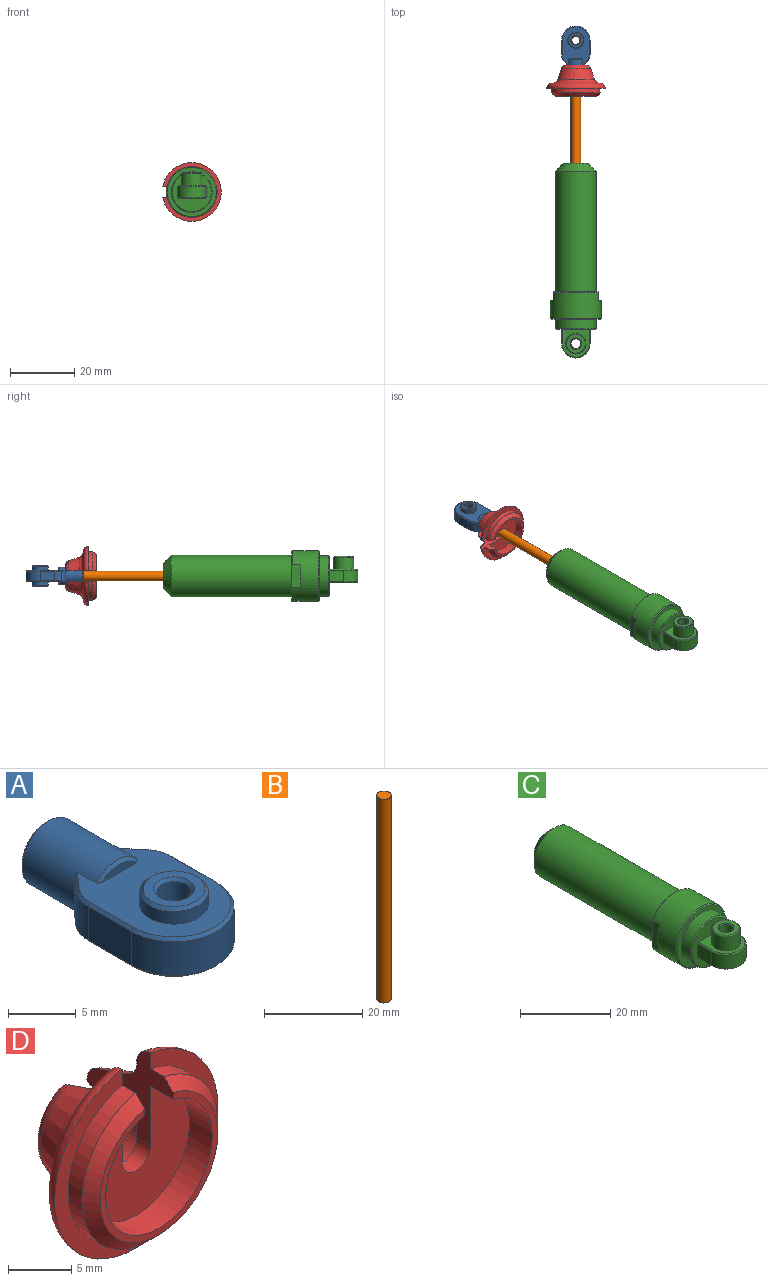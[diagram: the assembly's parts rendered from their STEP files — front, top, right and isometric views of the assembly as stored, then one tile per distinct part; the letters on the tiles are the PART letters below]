
ASSEMBLY  parts=4 mates=3
PART A: 42 faces, bbox 8.9x17.8x6.4 mm
  f0: cone r=2.67mm half-angle=45deg, axis (0,1,0), area 1.6mm2, adj f1,f23,f39
  f1: cylinder r=2.79mm len=7.11mm, axis (0,1,0), area 110.7mm2, adj f0,f2,f3,f16,f22,f23,f24,f30
  f2: cone r=2.67mm half-angle=45deg, axis (0,1,0), area 1.6mm2, adj f1,f38,f40
  f3: cone r=2.67mm half-angle=45deg, axis (0,-1,0), area 6mm2, adj f1,f4
  f4: plane 5.08x5.08mm, normal (0,1,0), area 10.6mm2, adj f3,f5
  f5: cone r=1.63mm half-angle=45deg, axis (0,1,0), area 3.7mm2, adj f4,f6
  f6: cylinder r=1.5mm len=7.37mm, axis (0,1,0), area 69.4mm2, adj f5,f41
  f7: cone r=2.41mm half-angle=45deg, axis (0,0,1), area 5.4mm2, adj f8,f9
  f8: plane 4.57x4.57mm, normal (0,0,-1), area 9.1mm2, adj f7,f10
  f9: cylinder r=2.54mm len=5.08mm, axis (0,0,-1), area 18.2mm2, adj f7,f23
  f10: cone r=1.4mm half-angle=45deg, axis (0,0,-1), area 3.2mm2, adj f8,f11
  f11: cylinder r=1.27mm len=5.84mm, axis (0,0,1), area 46.6mm2, adj f10,f15
  f12: cone r=2.41mm half-angle=45deg, axis (0,0,-1), area 5.4mm2, adj f13,f14
  f13: plane 4.57x4.57mm, normal (0,0,1), area 9.1mm2, adj f12,f15
  f14: cylinder r=2.54mm len=5.08mm, axis (0,0,1), area 18.2mm2, adj f12,f38
  f15: cone r=1.4mm half-angle=45deg, axis (0,0,1), area 3.2mm2, adj f11,f13
  f16: plane 1.67x1.51mm, normal (-0.53,0.47,-0.71), area 0.7mm2, adj f1,f17,f23,f37
  f17: cone r=3.05mm half-angle=45deg, axis (0,0,1), area 0.8mm2, adj f16,f18,f23,f36
  f18: plane 4.52x0.25mm, normal (-0.71,0,-0.71), area 1.6mm2, adj f17,f19,f23,f35
  f19: cone r=4.32mm half-angle=45deg, axis (0,0,1), area 4.9mm2, adj f18,f20,f23,f34
  f20: plane 4.52x0.25mm, normal (0.71,0,-0.71), area 1.6mm2, adj f19,f21,f23,f33
  f21: cone r=3.05mm half-angle=45deg, axis (0,0,1), area 0.8mm2, adj f20,f22,f23,f32
  f22: plane 1.67x1.51mm, normal (0.53,0.47,-0.71), area 0.7mm2, adj f1,f21,f23,f31
  f23: plane 12.14x8.4mm, normal (0,0,-1), area 59.3mm2, adj f0,f1,f9,f16,f17,f18,f19,f20
  f24: plane 1.67x1.51mm, normal (-0.53,0.47,0.71), area 0.7mm2, adj f1,f25,f37,f38
  f25: cone r=3.05mm half-angle=45deg, axis (0,0,-1), area 0.8mm2, adj f24,f26,f36,f38
  f26: plane 4.52x0.25mm, normal (-0.71,0,0.71), area 1.6mm2, adj f25,f27,f35,f38
  f27: cone r=4.32mm half-angle=45deg, axis (0,0,-1), area 4.9mm2, adj f26,f28,f34,f38
  f28: plane 4.52x0.25mm, normal (0.71,0,0.71), area 1.6mm2, adj f27,f29,f33,f38
  f29: cone r=3.05mm half-angle=45deg, axis (0,0,-1), area 0.8mm2, adj f28,f30,f32,f38
  f30: plane 1.67x1.51mm, normal (0.53,0.47,0.71), area 0.7mm2, adj f1,f29,f31,f38
  f31: plane 3.05x1.49mm, normal (0.75,0.66,0), area 4.6mm2, adj f1,f22,f30,f32
  f32: cylinder r=3.17mm len=3.05mm, axis (0,0,-1), area 7mm2, adj f21,f29,f31,f33
  f33: plane 4.52x3.05mm, normal (1,0,0), area 13.8mm2, adj f20,f28,f32,f34
  f34: cylinder r=4.45mm len=8.89mm, axis (0,0,1), area 42.6mm2, adj f19,f27,f33,f35
  f35: plane 4.52x3.05mm, normal (-1,0,0), area 13.8mm2, adj f18,f26,f34,f36
  f36: cylinder r=3.17mm len=3.05mm, axis (0,0,1), area 7mm2, adj f17,f25,f35,f37
  f37: plane 3.05x1.49mm, normal (-0.75,0.66,0), area 4.6mm2, adj f1,f16,f24,f36
  f38: plane 12.14x8.4mm, normal (0,0,1), area 59.3mm2, adj f1,f2,f14,f24,f25,f26,f27,f28
  f39: plane 3.63x0.76mm, normal (0,-1,0), area 1.9mm2, adj f0,f23
  f40: plane 3.63x0.76mm, normal (0,-1,0), area 1.9mm2, adj f2,f38
  f41: plane 3x3mm, normal (0,1,0), area 7.1mm2, adj f6
PART B: 3 faces, bbox 3x3x50.8 mm
  f0: cylinder r=1.5mm len=50.8mm, axis (0,0,-1), area 478.3mm2, adj f1,f2
  f1: plane 3x3mm, normal (0,0,1), area 7.1mm2, adj f0
  f2: plane 3x3mm, normal (0,0,-1), area 7.1mm2, adj f0
PART C: 35 faces, bbox 15.8x60.6x15.8 mm
  f0: cone r=1.63mm half-angle=45deg, axis (0,1,0), area 3.7mm2, adj f1,f2
  f1: cylinder r=1.5mm len=39.75mm, axis (0,1,0), area 374.3mm2, adj f0,f25
  f2: plane 7.75x7.75mm, normal (0,1,0), area 37.5mm2, adj f0,f26
  f3: cone r=7.75mm half-angle=45deg, axis (0,-1,0), area 6.3mm2, adj f4,f5,f28,f31
  f4: plane 7.29x2.56mm, normal (1,0,0), area 18.4mm2, adj f3,f5,f30,f31
  f5: cylinder r=7.87mm len=15.75mm, axis (0,1,0), area 365.7mm2, adj f3,f4,f11,f28,f29,f30,f31
  f6: cone r=3.05mm half-angle=45deg, axis (0,0,-1), area 6.9mm2, adj f7,f8
  f7: plane 5.84x5.84mm, normal (0,0,1), area 16.9mm2, adj f6,f9
  f8: cylinder r=3.17mm len=6.35mm, axis (0,0,1), area 76mm2, adj f6,f21
  f9: cone r=1.65mm half-angle=45deg, axis (0,0,1), area 3.7mm2, adj f7,f10
  f10: cylinder r=1.52mm len=7.75mm, axis (0,0,1), area 74.2mm2, adj f9,f16
  f11: cone r=7.75mm half-angle=45deg, axis (0,1,0), area 17.5mm2, adj f5,f12
  f12: plane 15.24x15.24mm, normal (0,-1,0), area 55.7mm2, adj f11,f15
  f13: cone r=6.22mm half-angle=45deg, axis (0,1,0), area 14mm2, adj f14,f15
  f14: plane 12.19x12.19mm, normal (0,-1,0), area 79.6mm2, adj f13,f17,f18,f20,f21,f22,f24,f32
  f15: cylinder r=6.35mm len=12.7mm, axis (0,1,0), area 116.5mm2, adj f12,f13
  f16: cone r=1.65mm half-angle=45deg, axis (0,0,-1), area 3.7mm2, adj f10,f17
  f17: plane 8.64x8.38mm, normal (0,0,-1), area 54.9mm2, adj f14,f16,f22,f23,f24
  f18: plane 4.45x0.25mm, normal (0.71,0,0.71), area 1.6mm2, adj f14,f19,f21,f34
  f19: cone r=4.32mm half-angle=45deg, axis (0,0,-1), area 4.9mm2, adj f18,f20,f21,f33
  f20: plane 4.45x0.25mm, normal (-0.71,0,0.71), area 1.6mm2, adj f14,f19,f21,f32
  f21: plane 8.64x8.38mm, normal (0,0,1), area 33.2mm2, adj f8,f14,f18,f19,f20
  f22: plane 4.45x0.25mm, normal (-0.71,0,-0.71), area 1.6mm2, adj f14,f17,f23,f32
  f23: cone r=4.32mm half-angle=45deg, axis (0,0,1), area 4.9mm2, adj f17,f22,f24,f33
  f24: plane 4.45x0.25mm, normal (0.71,0,-0.71), area 1.6mm2, adj f14,f17,f23,f34
  f25: plane 3x3mm, normal (0,1,0), area 7.1mm2, adj f1
  f26: cone r=5.14mm half-angle=45deg, axis (0,-1,0), area 116.1mm2, adj f2,f27
  f27: cylinder r=6.41mm len=37.47mm, axis (0,1,0), area 1509.7mm2, adj f26,f31
  f28: plane 7.29x2.56mm, normal (-1,0,0), area 18.4mm2, adj f3,f5,f29,f31
  f29: plane 7.27x0.89mm, normal (0,1,0), area 4.4mm2, adj f5,f28
  f30: plane 7.27x0.89mm, normal (0,1,0), area 4.4mm2, adj f4,f5
  f31: plane 15.49x13.97mm, normal (0,1,0), area 52.4mm2, adj f3,f4,f5,f27,f28
  f32: plane 4.45x3.68mm, normal (-1,0,0), area 16.4mm2, adj f14,f20,f22,f33
  f33: cylinder r=4.45mm len=8.89mm, axis (0,0,-1), area 51.4mm2, adj f19,f23,f32,f34
  f34: plane 4.45x3.68mm, normal (1,0,0), area 16.4mm2, adj f14,f18,f24,f33
PART D: 17 faces, bbox 20.1x10x19.9 mm
  f0: torus R=4.45mm, axis (0,1,0), area 17.2mm2, adj f1,f2,f4,f16
  f1: plane 9.94x9.32mm, normal (1,0,0), area 31.8mm2, adj f0,f2,f3,f5,f6,f7,f8,f9
  f2: torus R=3.23mm, axis (0,1,0), area 44.4mm2, adj f0,f1,f4,f15
  f3: torus R=7.56mm, axis (0,1,0), area 122.6mm2, adj f1,f4,f5,f11
  f4: plane 9.94x9.32mm, normal (-1,0,0), area 31.8mm2, adj f0,f2,f3,f5,f6,f7,f8,f9
  f5: plane 15.12x14.95mm, normal (0,1,0), area 8.1mm2, adj f1,f3,f4,f6
  f6: torus R=7.37mm, axis (0,1,0), area 74.9mm2, adj f1,f4,f5,f15
  f7: cone r=7.11mm half-angle=45deg, axis (0,1,0), area 59.6mm2, adj f1,f4,f8,f14
  f8: cylinder r=7.62mm len=15.24mm, axis (0,1,0), area 68.1mm2, adj f1,f4,f7,f11
  f9: cylinder r=1.59mm len=3.18mm, axis (0,-1,0), area 7.6mm2, adj f1,f4,f10,f12
  f10: plane 5.72x5.23mm, normal (0,1,0), area 13mm2, adj f1,f4,f9,f16
  f11: plane 18.29x18.15mm, normal (0,-1,0), area 75.4mm2, adj f1,f3,f4,f8
  f12: plane 11.94x11.72mm, normal (0,-1,0), area 89.1mm2, adj f1,f4,f9,f13
  f13: cylinder r=5.97mm len=11.94mm, axis (0,1,0), area 87.1mm2, adj f1,f4,f12,f14
  f14: plane 13.21x13.01mm, normal (0,-1,0), area 23mm2, adj f1,f4,f7,f13
  f15: cone r=5.3mm half-angle=18.2deg, axis (0,-1,0), area 107.8mm2, adj f1,f2,f4,f6
  f16: cylinder r=2.86mm len=5.72mm, axis (0,1,0), area 66.6mm2, adj f0,f1,f4,f10
PLACE A rot(axis=(1,0,0),180deg) t=(0,94.4,-2.1)mm
PLACE B rot(axis=(1,0,0),90deg) t=(0,37.88,-2.1)mm
PLACE C at identity fixed
PLACE D rot(axis=(0,-1,0),90deg) t=(0,81.06,-2.1)mm
MATE fastened B.f0 <-> A.f0  axis (0,1,0) through (0,88.68,-2.1)mm
MATE fastened D.f0 <-> A.f0  axis (0,1,0) through (0,81.06,-2.1)mm
MATE cylindrical B.f0 <-> C.f0  axis (0,1,0) through (0,37.88,-2.1)mm
